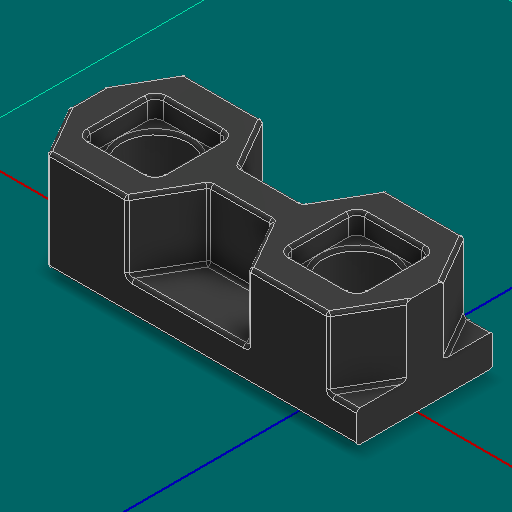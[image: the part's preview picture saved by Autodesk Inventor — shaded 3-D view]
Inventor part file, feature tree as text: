
AUTODESK INVENTOR PART (.ipt)
format: ipt  version: 2025 (Build 290162000, 162)  size: 399,872 bytes
history: native  units: in
note: dims shown in document units (in); Inventor stores cm internally (conversion verified against a paired STEP export)
features: other x3, sketch x2
ambient origin geometry x8: Origin, YZ Plane, XZ Plane, XY Plane, X Axis, Y Axis, Z Axis, Center Point
bodies: Solid1 (feature_tree)
feature tree (5):
  other  "Bearing Flat Low Profile 2-Hole.ipt"
  other  "Solid1::Bearing Flat Low Profile 2-Hole.ipt"
  other  "TaggingFeature1"
  sketch  "Sketch1"  dims[d0=0.3937in]
  sketch  "Sketch2"
